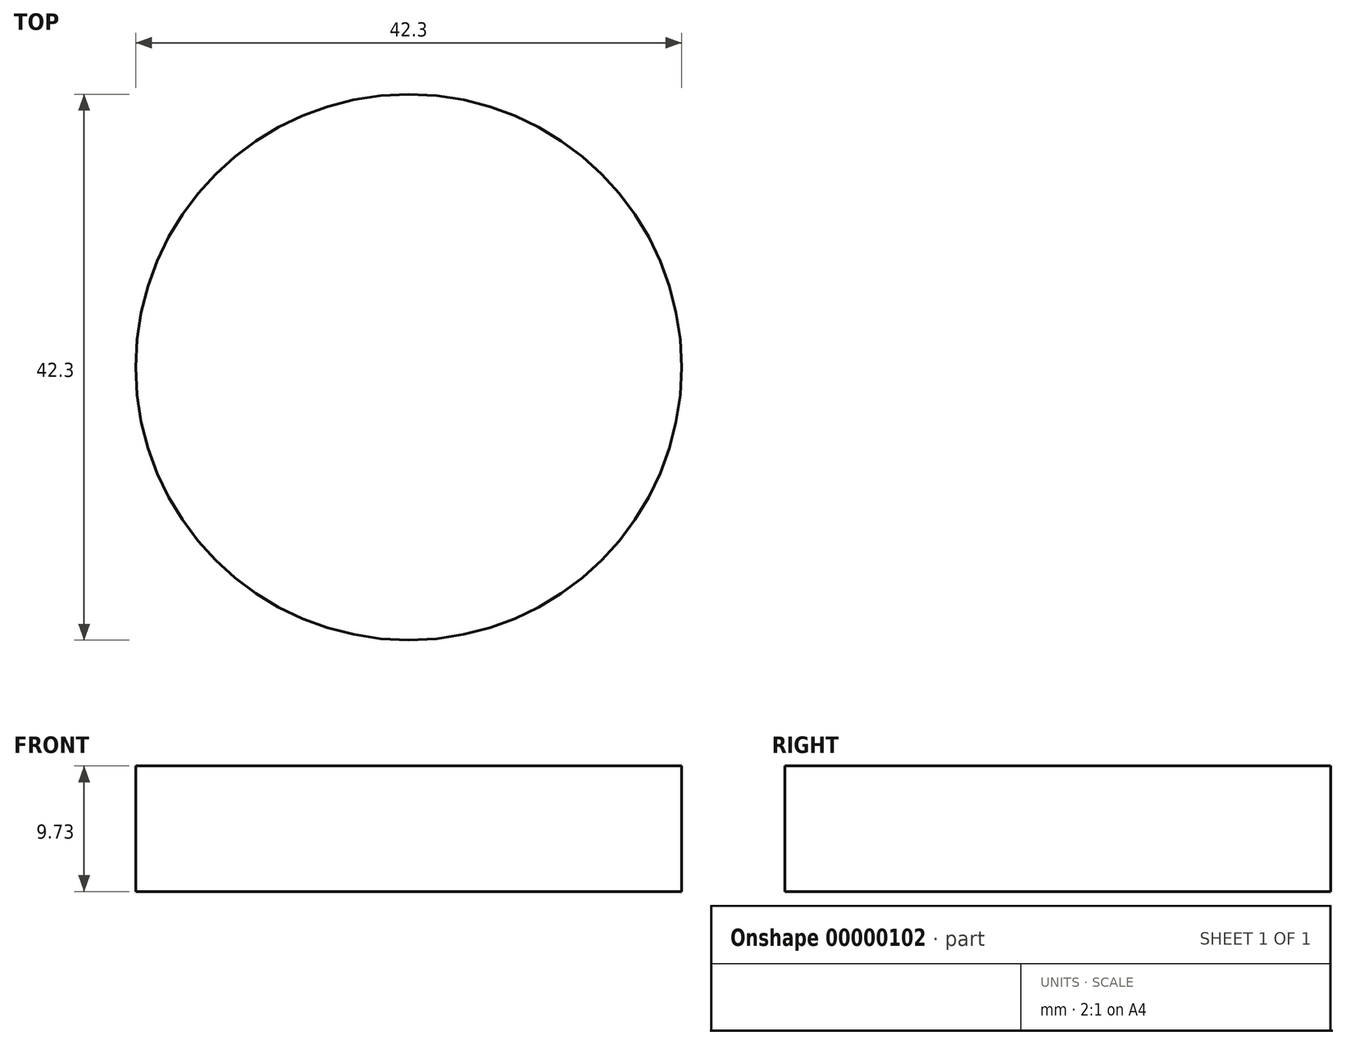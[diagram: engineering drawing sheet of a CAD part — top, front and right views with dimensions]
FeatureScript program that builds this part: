
annotation { "Feature Type Name" : "Feature", "Feature Type Description" : "" }
export const myFeature = defineFeature(function(context is Context, id is Id, definition is map)
    precondition{}
    {
        {
            var Q0;
            Q0=qCreatedBy(makeId("Top.planeOp"),FACE);
            var sketch = newSketch(context, id + "F0", { "sketchPlane" : qUnion([Q0])});
            skCircle(sketch, "E0", {"center": v(0, 0) * mm, "radius": 21.15 * mm});
            skSolve(sketch);
        }
        {
            var Q0;
            Q0=makeQuery(id+"F0.imprint","IMPRINT",FACE,{"disambiguationData":[TD([[makeQuery(id+"F0.imprint","IMPRINT",EDGE,{"derivedFrom":sQuery(id+"F0.wireOp",EDGE,"E0")}),1.0]])]});
            extrude(context, id + "F1", {"entities" : qUnion([Q0]), "oppositeDirection" : true, "depth" : 9.73 * mm});
        }
    });
